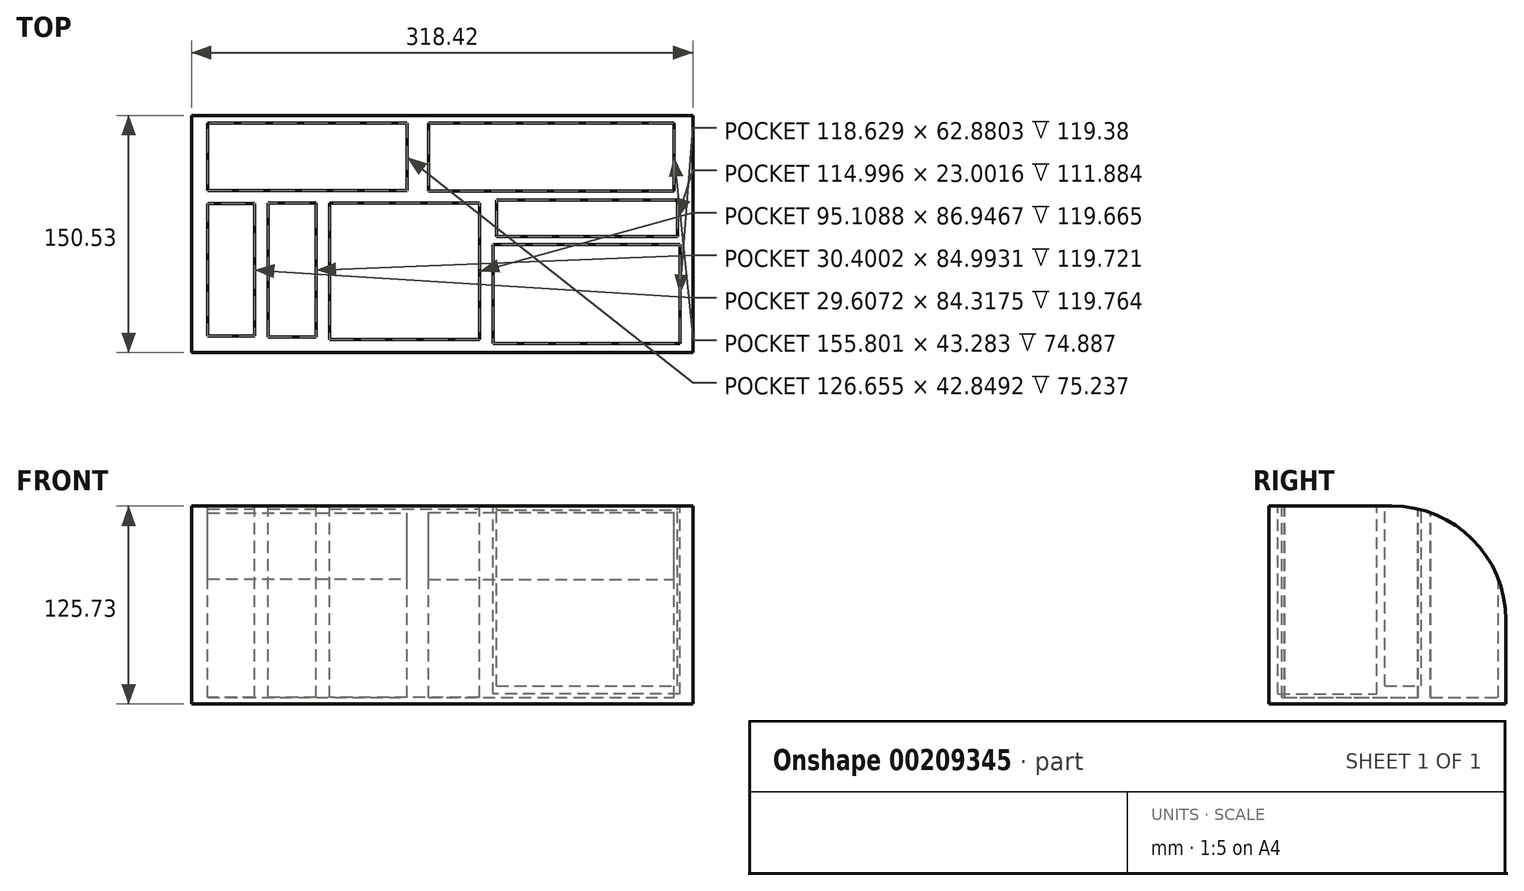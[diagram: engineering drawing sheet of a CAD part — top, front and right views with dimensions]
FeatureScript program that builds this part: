
annotation { "Feature Type Name" : "Feature", "Feature Type Description" : "" }
export const myFeature = defineFeature(function(context is Context, id is Id, definition is map)
    precondition{}
    {
        {
            var Q0;
            Q0=qCreatedBy(makeId("Top.planeOp"),FACE);
            var sketch = newSketch(context, id + "F0", { "sketchPlane" : qUnion([Q0])});
            skLineSegment(sketch, "E0.bottom", {"start": v(99.4, 42.12) * mm, "end": v(-99.4, 42.12) * mm});
            skLineSegment(sketch, "E0.top", {"start": v(99.4, -42.12) * mm, "end": v(-99.4, -42.12) * mm});
            skLineSegment(sketch, "E0.left", {"start": v(99.4, 42.12) * mm, "end": v(99.4, -42.12) * mm});
            skLineSegment(sketch, "E0.right", {"start": v(-99.4, 42.12) * mm, "end": v(-99.4, -42.12) * mm});
            skPoint(sketch, "E0.middle", {"position": v(0, 0) * mm});
            skSolve(sketch);
        }
        {
            var Q0;
            Q0=makeQuery(id+"F0.imprint","IMPRINT",FACE,{"disambiguationData":[TD([[makeQuery(id+"F0.imprint","IMPRINT",EDGE,{"derivedFrom":sQuery(id+"F0.wireOp",EDGE,"E0.bottom")}),1.0]])]});
            extrude(context, id + "F1", {"entities" : qUnion([Q0]), "depth" : 87.63 * mm});
        }
        {
            var Q0;
            Q0=makeQuery(id+"F1.opExtrude","SWEPT_FACE",FACE,{"disambiguationData":[OSD([sQuery(id+"F0.wireOp",EDGE,"E0.top")])]});
            extrude(context, id + "F2", {"entities" : qUnion([Q0]), "operationType" : NewBodyOperationType.ADD, "depth" : 30.23 * mm});
        }
        {
            var Q0;
            {var subQ0=sQuery(id+"F0.wireOp",EDGE,"E0.top");Q0=makeQuery(id+"F2.boolean.opBoolean","MERGE",FACE,{"derivedFrom":[makeQuery(id+"F1.opExtrude","CAP_FACE",FACE,{"disambiguationData":[OSD([sQuery(id+"F0.wireOp",EDGE,"E0.bottom"),subQ0,sQuery(id+"F0.wireOp",EDGE,"E0.left"),sQuery(id+"F0.wireOp",EDGE,"E0.right")])],"isStart":true}),makeQuery(id+"F2.opExtrude","SWEPT_FACE",FACE,{"disambiguationData":[OSD([subQ0]),TDD([makeQuery(id+"F1.opExtrude","CAP_EDGE",EDGE,{"disambiguationData":[OSD([subQ0])],"isStart":true})])]})]});}
            extrude(context, id + "F3", {"entities" : qUnion([Q0]), "operationType" : NewBodyOperationType.ADD, "depth" : 38.1 * mm});
        }
        {
            var Q0;
            {var subQ0=sQuery(id+"F0.wireOp",EDGE,"E0.top");Q0=makeQuery(id+"F3.boolean.opBoolean","MERGE",FACE,{"derivedFrom":[makeQuery(id+"F2.opExtrude","CAP_FACE",FACE,{"disambiguationData":[OSD([subQ0])],"isStart":false}),makeQuery(id+"F3.opExtrude","SWEPT_FACE",FACE,{"disambiguationData":[OSD([subQ0])]})]});}
            extrude(context, id + "F4", {"entities" : qUnion([Q0]), "operationType" : NewBodyOperationType.ADD, "depth" : 36.07 * mm});
        }
        {
            var Q0;
            {var subQ0=sQuery(id+"F0.wireOp",EDGE,"E0.top");var subQ1=makeQuery(id+"F1.opExtrude","CAP_EDGE",EDGE,{"disambiguationData":[OSD([subQ0])],"isStart":false});Q0=makeQuery(id+"F4.boolean.opBoolean","MERGE",FACE,{"derivedFrom":[makeQuery(id+"F2.boolean.opBoolean","MERGE",FACE,{"derivedFrom":[makeQuery(id+"F1.opExtrude","CAP_FACE",FACE,{"disambiguationData":[OSD([sQuery(id+"F0.wireOp",EDGE,"E0.bottom"),subQ0,sQuery(id+"F0.wireOp",EDGE,"E0.left"),sQuery(id+"F0.wireOp",EDGE,"E0.right")])],"isStart":false}),makeQuery(id+"F2.opExtrude","SWEPT_FACE",FACE,{"disambiguationData":[OSD([subQ0]),TDD([subQ1])]})]}),makeQuery(id+"F4.opExtrude","SWEPT_FACE",FACE,{"disambiguationData":[OSD([subQ0]),TDD([makeQuery(id+"F2.opExtrude","CAP_EDGE",EDGE,{"disambiguationData":[OSD([subQ0]),TDD([subQ1])],"isStart":false})])]})]});}
            var sketch = newSketch(context, id + "F5", { "sketchPlane" : qUnion([Q0])});
            skLineSegment(sketch, "E1.bottom", {"start": v(91.08, -102.67) * mm, "end": v(-27.54, -102.67) * mm});
            skLineSegment(sketch, "E1.top", {"start": v(91.08, -39.8) * mm, "end": v(-27.54, -39.8) * mm});
            skLineSegment(sketch, "E1.left", {"start": v(91.08, -102.67) * mm, "end": v(91.08, -39.8) * mm});
            skLineSegment(sketch, "E1.right", {"start": v(-27.54, -102.67) * mm, "end": v(-27.54, -39.8) * mm});
            skSolve(sketch);
        }
        {
            var Q0;
            Q0=makeQuery(id+"F5.imprint","IMPRINT",FACE,{"disambiguationData":[TD([[makeQuery(id+"F5.imprint","IMPRINT",EDGE,{"derivedFrom":sQuery(id+"F5.wireOp",EDGE,"E1.bottom")}),-1.0]])]});
            extrude(context, id + "F6", {"entities" : qUnion([Q0]), "operationType" : NewBodyOperationType.REMOVE, "oppositeDirection" : true, "depth" : 119.38 * mm});
        }
        {
            var Q0;
            {var subQ0=sQuery(id+"F0.wireOp",EDGE,"E0.top");var subQ1=makeQuery(id+"F1.opExtrude","CAP_EDGE",EDGE,{"disambiguationData":[OSD([subQ0])],"isStart":false});Q0=makeQuery(id+"F4.boolean.opBoolean","MERGE",FACE,{"derivedFrom":[makeQuery(id+"F2.boolean.opBoolean","MERGE",FACE,{"derivedFrom":[makeQuery(id+"F1.opExtrude","CAP_FACE",FACE,{"disambiguationData":[OSD([sQuery(id+"F0.wireOp",EDGE,"E0.bottom"),subQ0,sQuery(id+"F0.wireOp",EDGE,"E0.left"),sQuery(id+"F0.wireOp",EDGE,"E0.right")])],"isStart":false}),makeQuery(id+"F2.opExtrude","SWEPT_FACE",FACE,{"disambiguationData":[OSD([subQ0]),TDD([subQ1])]})]}),makeQuery(id+"F4.opExtrude","SWEPT_FACE",FACE,{"disambiguationData":[OSD([subQ0]),TDD([makeQuery(id+"F2.opExtrude","CAP_EDGE",EDGE,{"disambiguationData":[OSD([subQ0]),TDD([subQ1])],"isStart":false})])]})]});}
            var sketch = newSketch(context, id + "F7", { "sketchPlane" : qUnion([Q0])});
            skLineSegment(sketch, "E2.bottom", {"start": v(-25.36, -34.7) * mm, "end": v(89.64, -34.7) * mm});
            skLineSegment(sketch, "E2.top", {"start": v(-25.36, -11.7) * mm, "end": v(89.64, -11.7) * mm});
            skLineSegment(sketch, "E2.left", {"start": v(-25.36, -34.7) * mm, "end": v(-25.36, -11.7) * mm});
            skLineSegment(sketch, "E2.right", {"start": v(89.64, -34.7) * mm, "end": v(89.64, -11.7) * mm});
            skSolve(sketch);
        }
        {
            var Q0;
            Q0=makeQuery(id+"F7.imprint","IMPRINT",FACE,{"disambiguationData":[TD([[makeQuery(id+"F7.imprint","IMPRINT",EDGE,{"derivedFrom":sQuery(id+"F7.wireOp",EDGE,"E2.bottom")}),1.0]])]});
            extrude(context, id + "F8", {"entities" : qUnion([Q0]), "operationType" : NewBodyOperationType.REMOVE, "oppositeDirection" : true, "depth" : 114.3 * mm});
        }
        {
            var Q0;
            {var subQ0=sQuery(id+"F0.wireOp",EDGE,"E0.right");var subQ1=sQuery(id+"F0.wireOp",EDGE,"E0.top");Q0=makeQuery(id+"F4.boolean.opBoolean","MERGE",FACE,{"derivedFrom":[makeQuery(id+"F3.boolean.opBoolean","MERGE",FACE,{"derivedFrom":[makeQuery(id+"F2.boolean.opBoolean","MERGE",FACE,{"derivedFrom":[makeQuery(id+"F1.opExtrude","SWEPT_FACE",FACE,{"disambiguationData":[OSD([subQ0])]}),makeQuery(id+"F2.opExtrude","SWEPT_FACE",FACE,{"disambiguationData":[OSD([subQ1,subQ0])]})]}),makeQuery(id+"F3.opExtrude","SWEPT_FACE",FACE,{"disambiguationData":[OSD([subQ1,subQ0])]})]}),makeQuery(id+"F4.opExtrude","SWEPT_FACE",FACE,{"disambiguationData":[OSD([subQ1,subQ0])]})]});}
            extrude(context, id + "F9", {"entities" : qUnion([Q0]), "operationType" : NewBodyOperationType.ADD, "depth" : 216.92 * mm});
        }
        {
            var Q0;
            Q0=makeQuery(id+"F9.opExtrude","CAP_FACE",FACE,{"disambiguationData":[OSD([sQuery(id+"F0.wireOp",EDGE,"E0.top"),sQuery(id+"F0.wireOp",EDGE,"E0.right")])],"isStart":false});
            extrude(context, id + "F10", {"entities" : qUnion([Q0]), "operationType" : NewBodyOperationType.REMOVE, "oppositeDirection" : true, "depth" : 97.28 * mm});
        }
        {
            var Q0;
            {var subQ0=sQuery(id+"F0.wireOp",EDGE,"E0.right");var subQ1=sQuery(id+"F0.wireOp",EDGE,"E0.top");var subQ2=makeQuery(id+"F1.opExtrude","CAP_VERTEX",VERTEX,{"disambiguationData":[OSD([subQ1,subQ0])],"isStart":false});var subQ3=makeQuery(id+"F1.opExtrude","CAP_EDGE",EDGE,{"disambiguationData":[OSD([subQ1])],"isStart":false});Q0=makeQuery(id+"F9.boolean.opBoolean","MERGE",FACE,{"derivedFrom":[makeQuery(id+"F4.boolean.opBoolean","MERGE",FACE,{"derivedFrom":[makeQuery(id+"F2.boolean.opBoolean","MERGE",FACE,{"derivedFrom":[makeQuery(id+"F1.opExtrude","CAP_FACE",FACE,{"disambiguationData":[OSD([sQuery(id+"F0.wireOp",EDGE,"E0.bottom"),subQ1,sQuery(id+"F0.wireOp",EDGE,"E0.left"),subQ0])],"isStart":false}),makeQuery(id+"F2.opExtrude","SWEPT_FACE",FACE,{"disambiguationData":[OSD([subQ1]),TDD([subQ3])]})]}),makeQuery(id+"F4.opExtrude","SWEPT_FACE",FACE,{"disambiguationData":[OSD([subQ1]),TDD([makeQuery(id+"F2.opExtrude","CAP_EDGE",EDGE,{"disambiguationData":[OSD([subQ1]),TDD([subQ3])],"isStart":false})])]})]}),makeQuery(id+"F9.opExtrude","SWEPT_FACE",FACE,{"disambiguationData":[OSD([subQ1,subQ0]),TDD([makeQuery(id+"F4.boolean.opBoolean","MERGE",EDGE,{"derivedFrom":[makeQuery(id+"F2.boolean.opBoolean","MERGE",EDGE,{"derivedFrom":[makeQuery(id+"F1.opExtrude","CAP_EDGE",EDGE,{"disambiguationData":[OSD([subQ0])],"isStart":false}),makeQuery(id+"F2.opExtrude","SWEPT_EDGE",EDGE,{"disambiguationData":[OSD([subQ1,subQ0]),TDD([subQ2])]})]}),makeQuery(id+"F4.opExtrude","SWEPT_EDGE",EDGE,{"disambiguationData":[OSD([subQ1,subQ0]),TDD([makeQuery(id+"F2.opExtrude","CAP_VERTEX",VERTEX,{"disambiguationData":[OSD([subQ1,subQ0]),TDD([subQ2])],"isStart":false})])]})]})])]})]});}
            var sketch = newSketch(context, id + "F11", { "sketchPlane" : qUnion([Q0])});
            skLineSegment(sketch, "E3.bottom", {"start": v(-36.25, -100.29) * mm, "end": v(-131.35, -100.29) * mm});
            skLineSegment(sketch, "E3.top", {"start": v(-36.25, -13.34) * mm, "end": v(-131.35, -13.34) * mm});
            skLineSegment(sketch, "E3.left", {"start": v(-36.25, -100.29) * mm, "end": v(-36.25, -13.34) * mm});
            skLineSegment(sketch, "E3.right", {"start": v(-131.35, -100.29) * mm, "end": v(-131.35, -13.34) * mm});
            skSolve(sketch);
        }
        {
            var Q0;
            Q0=makeQuery(id+"F11.imprint","IMPRINT",FACE,{"disambiguationData":[TD([[makeQuery(id+"F11.imprint","IMPRINT",EDGE,{"derivedFrom":sQuery(id+"F11.wireOp",EDGE,"E3.bottom")}),1.0]])]});
            var sketch = newSketch(context, id + "F12", { "sketchPlane" : qUnion([Q0])});
            skLineSegment(sketch, "E4.bottom", {"start": v(-139.98, -98.57) * mm, "end": v(-170.38, -98.57) * mm});
            skLineSegment(sketch, "E4.top", {"start": v(-139.98, -13.58) * mm, "end": v(-170.38, -13.58) * mm});
            skLineSegment(sketch, "E4.left", {"start": v(-139.98, -98.57) * mm, "end": v(-139.98, -13.58) * mm});
            skLineSegment(sketch, "E4.right", {"start": v(-170.38, -98.57) * mm, "end": v(-170.38, -13.58) * mm});
            skSolve(sketch);
        }
        {
            var Q0;
            Q0=makeQuery(id+"F12.imprint","IMPRINT",FACE,{"disambiguationData":[TD([[makeQuery(id+"F12.imprint","IMPRINT",EDGE,{"derivedFrom":sQuery(id+"F12.wireOp",EDGE,"E4.bottom")}),1.0]])]});
            var sketch = newSketch(context, id + "F13", { "sketchPlane" : qUnion([Q0])});
            skLineSegment(sketch, "E5.bottom", {"start": v(-179.09, -98.08) * mm, "end": v(-208.7, -98.08) * mm});
            skLineSegment(sketch, "E5.top", {"start": v(-179.09, -13.76) * mm, "end": v(-208.7, -13.76) * mm});
            skLineSegment(sketch, "E5.left", {"start": v(-179.09, -98.08) * mm, "end": v(-179.09, -13.76) * mm});
            skLineSegment(sketch, "E5.right", {"start": v(-208.7, -98.08) * mm, "end": v(-208.7, -13.76) * mm});
            skSolve(sketch);
        }
        {
            var Q0;
            Q0=makeQuery(id+"F11.imprint","IMPRINT",FACE,{"disambiguationData":[TD([[makeQuery(id+"F11.imprint","IMPRINT",EDGE,{"derivedFrom":sQuery(id+"F11.wireOp",EDGE,"E3.bottom")}),-1.0]])]});
            extrude(context, id + "F14", {"entities" : qUnion([Q0]), "operationType" : NewBodyOperationType.REMOVE, "oppositeDirection" : true, "depth" : 121.67 * mm});
        }
        {
            var Q0;
            Q0=makeQuery(id+"F12.imprint","IMPRINT",FACE,{"disambiguationData":[TD([[makeQuery(id+"F12.imprint","IMPRINT",EDGE,{"derivedFrom":sQuery(id+"F12.wireOp",EDGE,"E4.bottom")}),-1.0]])]});
            extrude(context, id + "F15", {"entities" : qUnion([Q0]), "operationType" : NewBodyOperationType.REMOVE, "oppositeDirection" : true, "depth" : 121.67 * mm});
        }
        {
            var Q0;
            Q0=makeQuery(id+"F13.imprint","IMPRINT",FACE,{"disambiguationData":[TD([[makeQuery(id+"F13.imprint","IMPRINT",EDGE,{"derivedFrom":sQuery(id+"F13.wireOp",EDGE,"E5.bottom")}),-1.0]])]});
            extrude(context, id + "F16", {"entities" : qUnion([Q0]), "operationType" : NewBodyOperationType.REMOVE, "oppositeDirection" : true, "depth" : 121.67 * mm});
        }
        {
            var Q0;
            {var subQ0=sQuery(id+"F0.wireOp",EDGE,"E0.right");var subQ1=sQuery(id+"F0.wireOp",EDGE,"E0.top");var subQ2=makeQuery(id+"F1.opExtrude","CAP_VERTEX",VERTEX,{"disambiguationData":[OSD([subQ1,subQ0])],"isStart":false});var subQ3=makeQuery(id+"F1.opExtrude","CAP_EDGE",EDGE,{"disambiguationData":[OSD([subQ1])],"isStart":false});Q0=makeQuery(id+"F9.boolean.opBoolean","MERGE",FACE,{"derivedFrom":[makeQuery(id+"F4.boolean.opBoolean","MERGE",FACE,{"derivedFrom":[makeQuery(id+"F2.boolean.opBoolean","MERGE",FACE,{"derivedFrom":[makeQuery(id+"F1.opExtrude","CAP_FACE",FACE,{"disambiguationData":[OSD([sQuery(id+"F0.wireOp",EDGE,"E0.bottom"),subQ1,sQuery(id+"F0.wireOp",EDGE,"E0.left"),subQ0])],"isStart":false}),makeQuery(id+"F2.opExtrude","SWEPT_FACE",FACE,{"disambiguationData":[OSD([subQ1]),TDD([subQ3])]})]}),makeQuery(id+"F4.opExtrude","SWEPT_FACE",FACE,{"disambiguationData":[OSD([subQ1]),TDD([makeQuery(id+"F2.opExtrude","CAP_EDGE",EDGE,{"disambiguationData":[OSD([subQ1]),TDD([subQ3])],"isStart":false})])]})]}),makeQuery(id+"F9.opExtrude","SWEPT_FACE",FACE,{"disambiguationData":[OSD([subQ1,subQ0]),TDD([makeQuery(id+"F4.boolean.opBoolean","MERGE",EDGE,{"derivedFrom":[makeQuery(id+"F2.boolean.opBoolean","MERGE",EDGE,{"derivedFrom":[makeQuery(id+"F1.opExtrude","CAP_EDGE",EDGE,{"disambiguationData":[OSD([subQ0])],"isStart":false}),makeQuery(id+"F2.opExtrude","SWEPT_EDGE",EDGE,{"disambiguationData":[OSD([subQ1,subQ0]),TDD([subQ2])]})]}),makeQuery(id+"F4.opExtrude","SWEPT_EDGE",EDGE,{"disambiguationData":[OSD([subQ1,subQ0]),TDD([makeQuery(id+"F2.opExtrude","CAP_VERTEX",VERTEX,{"disambiguationData":[OSD([subQ1,subQ0]),TDD([subQ2])],"isStart":false})])]})]})])]})]});}
            var sketch = newSketch(context, id + "F17", { "sketchPlane" : qUnion([Q0])});
            skLineSegment(sketch, "E6.bottom", {"start": v(-208.7, -5.54) * mm, "end": v(-82.04, -5.54) * mm});
            skLineSegment(sketch, "E6.top", {"start": v(-208.7, 37.31) * mm, "end": v(-82.04, 37.31) * mm});
            skLineSegment(sketch, "E6.left", {"start": v(-208.7, -5.54) * mm, "end": v(-208.7, 37.31) * mm});
            skLineSegment(sketch, "E6.right", {"start": v(-82.04, -5.54) * mm, "end": v(-82.04, 37.31) * mm});
            skSolve(sketch);
        }
        {
            var Q0;
            Q0=makeQuery(id+"F17.imprint","IMPRINT",FACE,{"disambiguationData":[TD([[makeQuery(id+"F17.imprint","IMPRINT",EDGE,{"derivedFrom":sQuery(id+"F17.wireOp",EDGE,"E6.bottom")}),-1.0]])]});
            var sketch = newSketch(context, id + "F18", { "sketchPlane" : qUnion([Q0])});
            skLineSegment(sketch, "E7.bottom", {"start": v(-68.43, -5.84) * mm, "end": v(87.37, -5.84) * mm});
            skLineSegment(sketch, "E7.top", {"start": v(-68.43, 37.45) * mm, "end": v(87.37, 37.45) * mm});
            skLineSegment(sketch, "E7.left", {"start": v(-68.43, -5.84) * mm, "end": v(-68.43, 37.45) * mm});
            skLineSegment(sketch, "E7.right", {"start": v(87.37, -5.84) * mm, "end": v(87.37, 37.45) * mm});
            skSolve(sketch);
        }
        {
            var Q0;
            Q0=makeQuery(id+"F18.imprint","IMPRINT",FACE,{"disambiguationData":[TD([[makeQuery(id+"F18.imprint","IMPRINT",EDGE,{"derivedFrom":sQuery(id+"F18.wireOp",EDGE,"E7.bottom")}),1.0]])]});
            extrude(context, id + "F19", {"entities" : qUnion([Q0]), "operationType" : NewBodyOperationType.REMOVE, "oppositeDirection" : true, "depth" : 121.67 * mm});
        }
        {
            var Q0;
            Q0=makeQuery(id+"F17.imprint","IMPRINT",FACE,{"disambiguationData":[TD([[makeQuery(id+"F17.imprint","IMPRINT",EDGE,{"derivedFrom":sQuery(id+"F17.wireOp",EDGE,"E6.bottom")}),1.0]])]});
            extrude(context, id + "F20", {"entities" : qUnion([Q0]), "operationType" : NewBodyOperationType.REMOVE, "oppositeDirection" : true, "depth" : 121.67 * mm});
        }
        {
            var Q0;
            {var subQ0=sQuery(id+"F0.wireOp",EDGE,"E0.right");var subQ1=sQuery(id+"F0.wireOp",EDGE,"E0.bottom");Q0=makeQuery(id+"F9.boolean.opBoolean","MERGE",EDGE,{"derivedFrom":[makeQuery(id+"F1.opExtrude","CAP_EDGE",EDGE,{"disambiguationData":[OSD([subQ1])],"isStart":false}),makeQuery(id+"F9.opExtrude","SWEPT_EDGE",EDGE,{"disambiguationData":[OSD([subQ1,subQ0]),TDD([makeQuery(id+"F1.opExtrude","CAP_VERTEX",VERTEX,{"disambiguationData":[OSD([subQ1,subQ0])],"isStart":false})])]})]});}
            fillet(context, id + "F21", {"entities" : qUnion([Q0]), "radius" : 72.36 * mm, "tangentPropagation" : true, "allowEdgeOverflow" : false});
        }
    });
